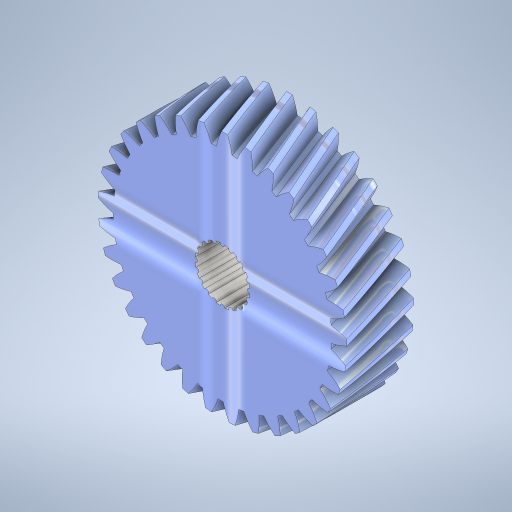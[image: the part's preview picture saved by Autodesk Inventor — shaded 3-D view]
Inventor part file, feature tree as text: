
AUTODESK INVENTOR PART (.ipt)
format: ipt  version: 2024 (Build 280153000, 153)  size: 860,160 bytes
history: native  units: mm (DEFAULTED — no unit token found)
features: plane x3, other x3, extrude x2, sketch x1
ambient origin geometry x8: Origin, YZ Plane, XZ Plane, XY Plane, X Axis, Y Axis, Z Axis, Center Point
bodies: Solid1 (feature_tree)
feature tree (9):
  extrude  "Extrusion1"  Depth=15.0mm TaperAngle=0.0deg
  plane  "Work Plane2"
  plane  "Work Plane8"
  plane  "Work Plane9"
  other  "Spur Gear"
  extrude  "Extrusion2"  Depth=0.515mm
  sketch  "Sketch1"  dims[d0=55.6768mm d1=15.0mm d2=0.0mm d3=52.6768mm d4=10.0mm d5=0.0mm d16=63.909111mm d17=0.0mm d34=0.951998mm d39=0.0mm d41=0.0mm d43=63.909111mm d46=63.909111mm d47=0.0mm d48=0.0mm d49=12.217mm d50=0.0mm d51=0.0mm d52=0.515mm d53=6.1135mm d54=200.0mm d56=360.0deg]
  other  "Srf1"
  other  "Pitch Diameter"
